# Revit family: IS_Conca_T4333_BIM_IT
name_source: partatom
category: Plumbing Fixtures
revit_build: Autodesk Revit 2017 (Build: 20160225_1515(x64)
units: mm (PartAtom-declared; Revit-internal decimal feet)

## family parameters
Always vertical = No
Cut with Voids When Loaded = No
OmniClass Number = 23.45.05.14.21.11
OmniClass Title = Bath/Shower Units
Part Type = Normal
Room Calculation Point = No
Round Connector Dimension = Use Diameter
Shared = No
Work Plane-Based = No

## types (6) — shared parameters
Accessori = https://www.idealstandard.it
Aiuto = https://www.idealstandard.it
AltezzaNominale = 360 mm  [stored 1.1811 ft]
Autore = Ideal Standard
BIMobject category = Storage
BIMobject category code = sanitary-storage
BIMobject main category = Sanitary
BIMobject main category code = sanitary
Brand = https://www.idealstandard.it
DescrizioneClassifcazioneUni2015 = Bathroom cabinets
DurataGaranzia = 2
DurataGaranziaProdotti = 2
Forma = Rettangolare
Garanzia = Garanzia Idealstandard
IfcEsportaCome = IfcFurnitureType
InformaziniGaranzia = https://www.idealstandard.it
InformazioniDiProdotto = http://www.idealstandard.it
InformazioniGaranzia = https://www.idealstandard.it
Installation instructions = https://www.idealspec.co.uk
InstruzioniInstallazione = https://www.idealstandard.it
LarghezzaNominale = 2387 mm  [stored 7.83136 ft]
Maniglia = No
Manufacturer = Ideal Standard
Materiale = Ceramics
NettWeight = 68.5
NominalDepth = 505 mm  [stored 1.65682 ft]
NominalHeight = 360 mm  [stored 1.1811 ft]
NominalWidth = 2384 mm
PesoNetto = 68.5
PiattoDoccia = No
Product group = Bathroom_Furniture
Produttore = Ideal Standard
ProfonditaNominale = 505 mm  [stored 1.65682 ft]
Revisione = 1
RiferimentoClassificazioneUni2015 = Pr_40_30_78_03
Spazio = Interno
Telefono = 800 652 290
TipoEspotazioneIfc = Bathroom cabinets
URL = https://www.ideal-standard.co.uk
Uniclass 2015 Code = Pr_40_30_78_03
Uniclass 2015 Name = Bathroom cabinets
UnitàDurata = Anno
UnitàDurataGaranzia = Anno
UnitàLineare = Milimitre
UnitàMonetaria = €
UnitàSuperficie = Milimitre
UnitàVolume = Litri
Versione = 1
VersioneClassificazioneUni2015 = v1.1
zero-valued in all types: CostoDiSostituzione, DimensioneScarico, LunghezzaNominale, Nominal depth, Nominal height, NominalLength, SeatMaterial, SpessoreDelMateriale, SpilloverLivello, Weight Net (Kg)

## per-type parameters (varying)
| type | Caratteristiche | CodiceABarre | CodiceArticolo | Colore | Description | Desrizione | Finitura | Model | ModelNumber | ModelloDiRiferimento | Nome | NomeOggettoBim | NumeroDiModello |
| T4333Y1 - BSN UN 240X50X37 2 DR  NOWTOP WHMT | Mobile sottolavabo, 2400x 372 x 550mm senza piano da appoggio per l'abbinamento ai piani in gres porcellanato o alle mensole  con 2 cassetti esterni. Dotato di tecnologia push open e soft close. Cassetti in metallo . Finitura Bianco laccato opaco | 8014140464693 | T4333Y1 | Matt white | Vanity unit, 2400x 372 x 550mm without countertop to combine with porcelain stoneware tops or shelves with 2 external drawers. Equipped with push open and soft close technology.  Matt white lacquered finish | Mobile sottolavabo, 2400x 372 x 550mm senza piano da appoggio per l'abbinamento ai piani in gres porcellanato o alle mensole  con 2 cassetti esterni. Dotato di tecnologia push open e soft close. Cassetti in metallo . Finitura Bianco laccato opaco | Matt white | T4333Y1 | T4333Y1 | T4333Y1 | BathroomCabinets_Conca_T4333Y1_IdealStandard | ISI_IdealStandard_Bathroom Cabinets_Conca_T4333Y1 | T4333Y1 |
| T4333Y2 - BSN UN 240X50X37 2 DR  NOWTOP ANMT | Mobile sottolavabo, 2400x 372 x 550mm senza piano da appoggio per l'abbinamento ai piani in gres porcellanato o alle mensole  con 2 cassetti esterni. Dotato di tecnologia push open e soft close. Cassetti in metallo. Finitura Antracite laccato opaco | 8014140464709 | T4333Y2 | Matt anthracite | Vanity unit, 2400x 372 x 550mm without countertop to combine with porcelain stoneware tops or shelves with 2 external drawers. Equipped with push open and soft close technology.  Anthracite matt lacquer finish | Mobile sottolavabo, 2400x 372 x 550mm senza piano da appoggio per l'abbinamento ai piani in gres porcellanato o alle mensole  con 2 cassetti esterni. Dotato di tecnologia push open e soft close. Cassetti in metallo. Finitura Antracite laccato opaco | Matt anthracite | T4333Y2 | T4333Y2 | T4333Y2 | BathroomCabinets_Conca_T4333Y2_IdealStandard | ISI_IdealStandard_Bathroom Cabinets_Conca_T4333Y2 | T4333Y2 |
| T4333Y3 - BSN UN 240X50X37 2 DR  NOWTOP SNMT | Mobile sottolavabo, 2400x 372 x 550mm senza piano da appoggio per l'abbinamento ai piani in gres porcellanato o alle mensole  con 2 cassetti esterni. Dotato di tecnologia push open e soft close. Cassetti in metallo. Finitura Sunset laccato opaco | 8014140464716 | T4333Y3 | Matt Sunset | Vanity unit, 2400x 372 x 550mm without countertop to combine with porcelain stoneware tops or shelves with 2 external drawers. Equipped with push open and soft close technology.  Sunset matt lacquer finish | Mobile sottolavabo, 2400x 372 x 550mm senza piano da appoggio per l'abbinamento ai piani in gres porcellanato o alle mensole  con 2 cassetti esterni. Dotato di tecnologia push open e soft close. Cassetti in metallo. Finitura Sunset laccato opaco | Matt Sunset | T4333Y3 | T4333Y3 | T4333Y3 | BathroomCabinets_Conca_T4333Y3_IdealStandard | ISI_IdealStandard_Bathroom Cabinets_Conca_T4333Y3 | T4333Y3 |
| T4333Y4 - BSN UN 240X50X37 2 DR  NOWTOP SMOK | Mobile sottolavabo, 2400x 372 x 550mm senza piano da appoggio per l'abbinamento ai piani in gres porcellanato o alle mensole  con 2 cassetti esterni. Dotato di tecnologia push open e soft close. Cassetti in metallo. Finitura Rovere affumicato scuro | 8014140464723 | T4333Y4 | Smoked Oak | Vanity unit, 2400x 372 x 550mm without countertop to combine with porcelain stoneware tops or shelves with 2 external drawers. Equipped with push open and soft close technology.  Dark smoked oak finish | Mobile sottolavabo, 2400x 372 x 550mm senza piano da appoggio per l'abbinamento ai piani in gres porcellanato o alle mensole  con 2 cassetti esterni. Dotato di tecnologia push open e soft close. Cassetti in metallo. Finitura Rovere affumicato scuro | Smoked Oak | T4333Y4 | T4333Y4 | T4333Y4 | BathroomCabinets_Conca_T4333Y4_IdealStandard | ISI_IdealStandard_Bathroom Cabinets_Conca_T4333Y4 | T4333Y4 |
| T4333Y5 - BSN UN 240X50X37 2 DR  NOWTOP DKWN | Mobile sottolavabo, 2400x 372 x 550mm senza piano da appoggio per l'abbinamento ai piani in gres porcellanato o alle mensole  con 2 cassetti esterni. Dotato di tecnologia push open e soft close. Cassetti in metallo. Finitura Noce scuro | 8014140464730 | T4333Y5 | Dark Walnut | Vanity unit, 2400x 372 x 550mm without countertop to combine with porcelain stoneware tops or shelves with 2 external drawers. Equipped with push open and soft close technology.  Dark Walnut finish | Mobile sottolavabo, 2400x 372 x 550mm senza piano da appoggio per l'abbinamento ai piani in gres porcellanato o alle mensole  con 2 cassetti esterni. Dotato di tecnologia push open e soft close. Cassetti in metallo. Finitura Noce scuro | Dark Walnut | T4333Y5 | T4333Y5 | T4333Y5 | BathroomCabinets_Conca_T4333Y5_IdealStandard | ISI_IdealStandard_Bathroom Cabinets_Conca_T4333Y5 | T4333Y5 |
| T4333Y6 - BSN UN 240X50X37 2 DR  NOWTOP LTOK | Mobile sottolavabo, 2400x 372 x 550mm senza piano da appoggio per l'abbinamento ai piani in gres porcellanato o alle mensole  con 2 cassetti esterni. Dotato di tecnologia push open e soft close. Cassetti in metallo. Finitura Legno chiaro | 8014140464747 | T4333Y6 | Light Oak | Vanity unit, 2400x 372 x 550mm without countertop to combine with porcelain stoneware tops or shelves with 2 external drawers. Equipped with push open and soft close technology.  Light wood finish | Mobile sottolavabo, 2400x 372 x 550mm senza piano da appoggio per l'abbinamento ai piani in gres porcellanato o alle mensole  con 2 cassetti esterni. Dotato di tecnologia push open e soft close. Cassetti in metallo. Finitura Legno chiaro | Light Oak | T4333Y6 | T4333Y6 | T4333Y6 | BathroomCabinets_Conca_T4333Y6_IdealStandard | ISI_IdealStandard_Bathroom Cabinets_Conca_T4333Y6 | T4333Y6 |

note: [stored X ft] marks values corroborated as IEEE doubles in the binary element streams (Revit-internal decimal feet)

## geometry (parser evidence)
native form markers: Sweep x4
no freeform markers — native parametric forms only
